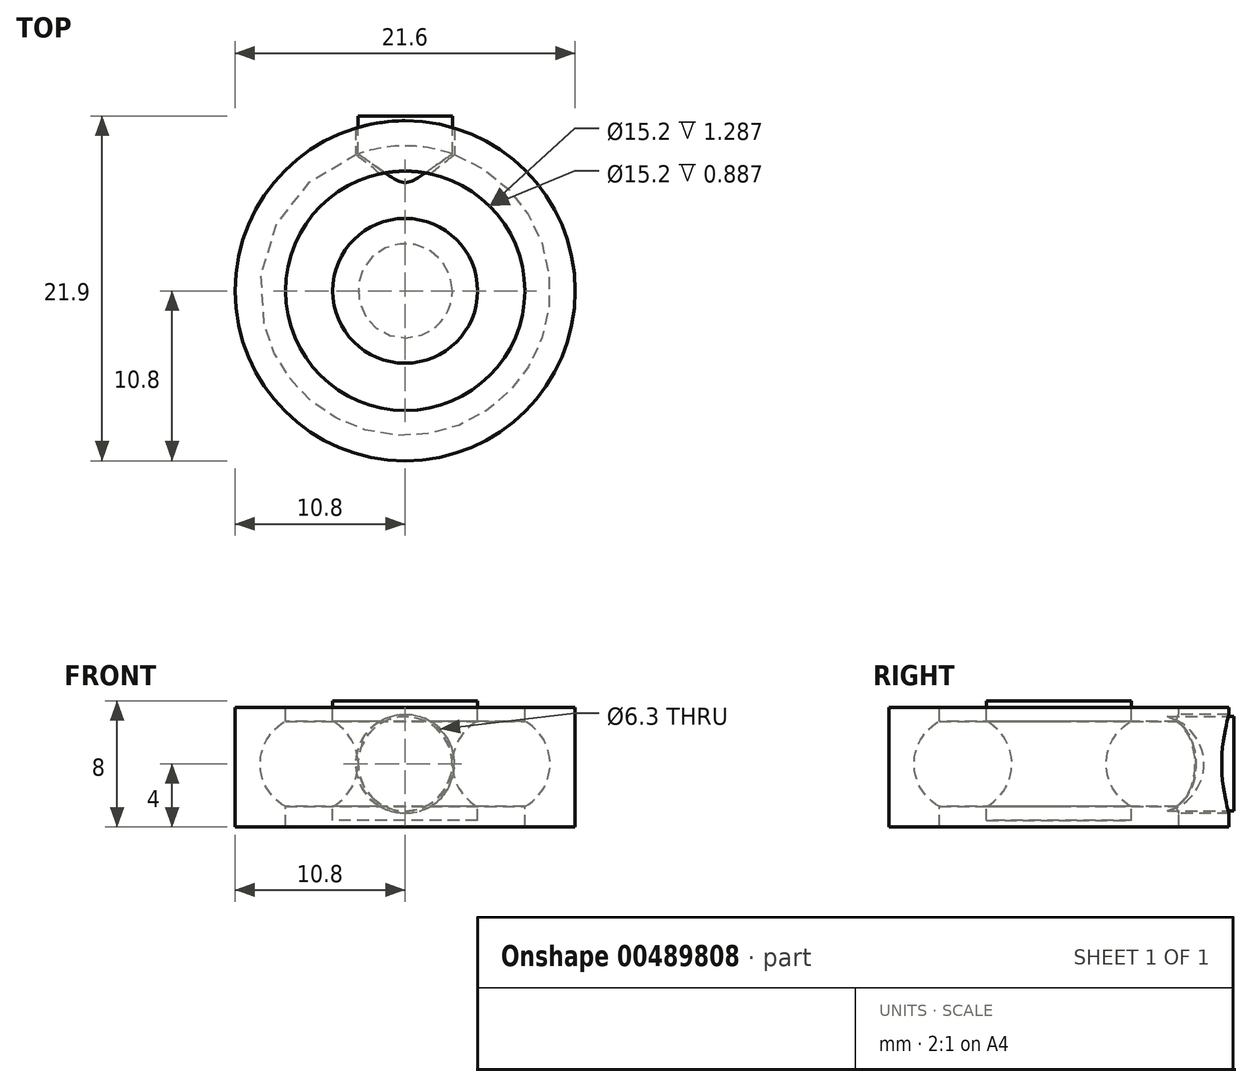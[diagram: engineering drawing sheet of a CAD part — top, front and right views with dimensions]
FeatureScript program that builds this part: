
annotation { "Feature Type Name" : "Feature", "Feature Type Description" : "" }
export const myFeature = defineFeature(function(context is Context, id is Id, definition is map)
    precondition{}
    {
        {
            var Q0;
            Q0=qCreatedBy(makeId("Top.planeOp"),FACE);
            var sketch = newSketch(context, id + "F0", { "sketchPlane" : qUnion([Q0])});
            skArc(sketch, "E0", {"start": v(3, 0) * mm, "mid": v(0, 3) * mm, "end": v(-3, 0) * mm});
            skLineSegment(sketch, "E1", {"start": v(3, 0) * mm, "end": v(-3, 0) * mm});
            skLineSegment(sketch, "E2", {"start": v(0, 0) * mm, "end": v(0, -6.1) * mm, "construction": true});
            skSolve(sketch);
        }
        {
            var Q0;
            Q0=qCreatedBy(makeId("Right.planeOp"),FACE);
            var sketch = newSketch(context, id + "F1", { "sketchPlane" : qUnion([Q0])});
            skCircle(sketch, "E3", {"center": v(0, 0) * mm, "radius": 3.1 * mm});
            skLineSegment(sketch, "E4", {"start": v(0, 0) * mm, "end": v(-12.4, 0) * mm, "construction": true});
            skLineSegment(sketch, "E5", {"start": v(-12.4, 8.14) * mm, "end": v(-12.4, -5.03) * mm, "construction": true});
            skLineSegment(sketch, "E6", {"start": v(0, 0) * mm, "end": v(0, 3.76) * mm, "construction": true});
            skLineSegment(sketch, "E7", {"start": v(-6.1, 3.76) * mm, "end": v(-6.1, -2.41) * mm, "construction": true});
            skSolve(sketch);
        }
        {
            var Q0;
            Q0=sQuery(id+"F1.wireOp",EDGE,"E3");
            var Q1;
            Q1=sQuery(id+"F1.wireOp",EDGE,"E7");
            revolve(context, id + "F2", {"bodyType" : ExtendedToolBodyType.SURFACE, "surfaceEntities" : qUnion([Q0]), "axis" : qUnion([Q1]), "revolveType" : RevolveType.FULL});
        }
        {
            var Q0;
            Q0=qCreatedBy(makeId("Right.planeOp"),FACE);
            var sketch = newSketch(context, id + "F3", { "sketchPlane" : qUnion([Q0])});
            skCircle(sketch, "E8.0", {"center": v(0, 0) * mm, "radius": 3.1 * mm});
            skLineSegment(sketch, "E9.0", {"start": v(-6.1, 3.76) * mm, "end": v(-6.1, -2.41) * mm});
            skLineSegment(sketch, "E9.1", {"start": v(0, 0) * mm, "end": v(-12.4, 0) * mm});
            skPoint(sketch, "E10.rect.middle", {"position": v(-6.1, 0) * mm});
            skLineSegment(sketch, "E11", {"start": v(-1.5, 4) * mm, "end": v(-1.5, -3.6) * mm});
            skLineSegment(sketch, "E12", {"start": v(-1.5, -3.6) * mm, "end": v(-6.1, -3.6) * mm});
            skLineSegment(sketch, "E13", {"start": v(-6.1, -3.6) * mm, "end": v(-6.1, 4) * mm});
            skLineSegment(sketch, "E14", {"start": v(-6.1, 4) * mm, "end": v(-1.5, 4) * mm});
            skLineSegment(sketch, "E15", {"start": v(4.7, 3.6) * mm, "end": v(4.7, -4) * mm});
            skLineSegment(sketch, "E16", {"start": v(4.7, -4) * mm, "end": v(1.5, -4) * mm});
            skLineSegment(sketch, "E17", {"start": v(4.7, 3.6) * mm, "end": v(1.5, 3.6) * mm});
            skLineSegment(sketch, "E18", {"start": v(1.5, 3.6) * mm, "end": v(1.5, -4) * mm});
            skSolve(sketch);
        }
        {
            var Q0;
            {var subQ0=sQuery(id+"F3.wireOp",EDGE,"E14");Q0=makeQuery(id+"F3.imprint","IMPRINT",FACE,{"disambiguationData":[TD([[makeQuery(id+"F3.imprint","IMPRINT",EDGE,{"derivedFrom":subQ0}),-1.0]])]});}
            var Q1;
            {var subQ3=sQuery(id+"F3.wireOp",EDGE,"E12");Q1=makeQuery(id+"F3.imprint","IMPRINT",FACE,{"disambiguationData":[TD([[makeQuery(id+"F3.imprint","IMPRINT",EDGE,{"derivedFrom":subQ3}),-1.0]])]});}
            var Q2;
            Q2=sQuery(id+"F3.wireOp",EDGE,"E9.0");
            revolve(context, id + "F4", {"entities" : qUnion([Q0, Q1]), "axis" : qUnion([Q2]), "revolveType" : RevolveType.FULL});
        }
        {
            var Q0;
            Q0=makeQuery(id+"F3.imprint","IMPRINT",FACE,{"disambiguationData":[TD([[makeQuery(id+"F3.imprint","IMPRINT",EDGE,{"derivedFrom":sQuery(id+"F3.wireOp",EDGE,"E15")}),-1.0]])]});
            var Q1;
            Q1=sQuery(id+"F3.wireOp",EDGE,"E9.0");
            revolve(context, id + "F5", {"entities" : qUnion([Q0]), "axis" : qUnion([Q1]), "revolveType" : RevolveType.FULL});
        }
        {
            var Q0;
            Q0=qCreatedBy(makeId("Front.planeOp"),FACE);
            var sketch = newSketch(context, id + "F6", { "sketchPlane" : qUnion([Q0])});
            skCircle(sketch, "E19", {"center": v(0, 0) * mm, "radius": 3.15 * mm});
            skSolve(sketch);
        }
        {
            var Q0;
            Q0=makeQuery(id+"F6.imprint","IMPRINT",FACE,{"disambiguationData":[TD([[makeQuery(id+"F6.imprint","IMPRINT",EDGE,{"derivedFrom":sQuery(id+"F6.wireOp",EDGE,"E19")}),1.0]])]});
            var Q1;
            Q1=makeQuery(id+"F5.opRevolve","SWEPT_FACE",FACE,{"disambiguationData":[OSD([sQuery(id+"F3.wireOp",EDGE,"E15")])]});
            extrude(context, id + "F7", {"entities" : qUnion([Q0]), "operationType" : NewBodyOperationType.REMOVE, "endBound" : BoundingType.UP_TO_SURFACE, "oppositeDirection" : true, "endBoundEntityFace" : qUnion([Q1]), "depth" : 25 * mm});
        }
        {
            var Q0;
            Q0=qCreatedBy(makeId("Front.planeOp"),FACE);
            var sketch = newSketch(context, id + "F8", { "sketchPlane" : qUnion([Q0])});
            skLineSegment(sketch, "E20.rect.bottom", {"start": v(13.05, 1.97) * mm, "end": v(8.99, 1.97) * mm});
            skLineSegment(sketch, "E20.rect.top", {"start": v(13.05, 8.89) * mm, "end": v(8.99, 8.89) * mm});
            skLineSegment(sketch, "E20.rect.left", {"start": v(13.05, 1.97) * mm, "end": v(13.05, 8.89) * mm});
            skLineSegment(sketch, "E20.rect.right", {"start": v(8.99, 1.97) * mm, "end": v(8.99, 8.89) * mm});
            skPoint(sketch, "E20.rect.middle", {"position": v(11.02, 5.43) * mm});
            skSolve(sketch);
        }
        {
            var Q0;
            Q0=makeQuery(id+"F8.imprint","IMPRINT",FACE,{"disambiguationData":[TD([[makeQuery(id+"F8.imprint","IMPRINT",EDGE,{"derivedFrom":sQuery(id+"F8.wireOp",EDGE,"E20.rect.bottom")}),-1.0]])]});
            cPlane(context, id + "F9", {"entities" : qUnion([Q0]), "cplaneType" : CPlaneType.OFFSET, "offset" : 5 * mm, "oppositeDirection" : true, "width" : 150 * mm, "height" : 150 * mm});
        }
        {
            var Q0;
            Q0=qCreatedBy(id+"F9.planeOp",FACE);
            var sketch = newSketch(context, id + "F10", { "sketchPlane" : qUnion([Q0])});
            skCircle(sketch, "E21", {"center": v(0, 0) * mm, "radius": 3 * mm});
            skSolve(sketch);
        }
        {
            var Q0;
            Q0=makeQuery(id+"F10.imprint","IMPRINT",FACE,{"disambiguationData":[TD([[makeQuery(id+"F10.imprint","IMPRINT",EDGE,{"derivedFrom":sQuery(id+"F10.wireOp",EDGE,"E21")}),1.0]])]});
            var Q1;
            Q1=makeQuery(id+"F5.opRevolve","SWEPT_FACE",FACE,{"disambiguationData":[OSD([sQuery(id+"F3.wireOp",EDGE,"E8.0")])]});
            extrude(context, id + "F11", {"entities" : qUnion([Q0]), "endBound" : BoundingType.UP_TO_SURFACE, "endBoundEntityFace" : qUnion([Q1]), "depth" : 25 * mm});
        }
    });
